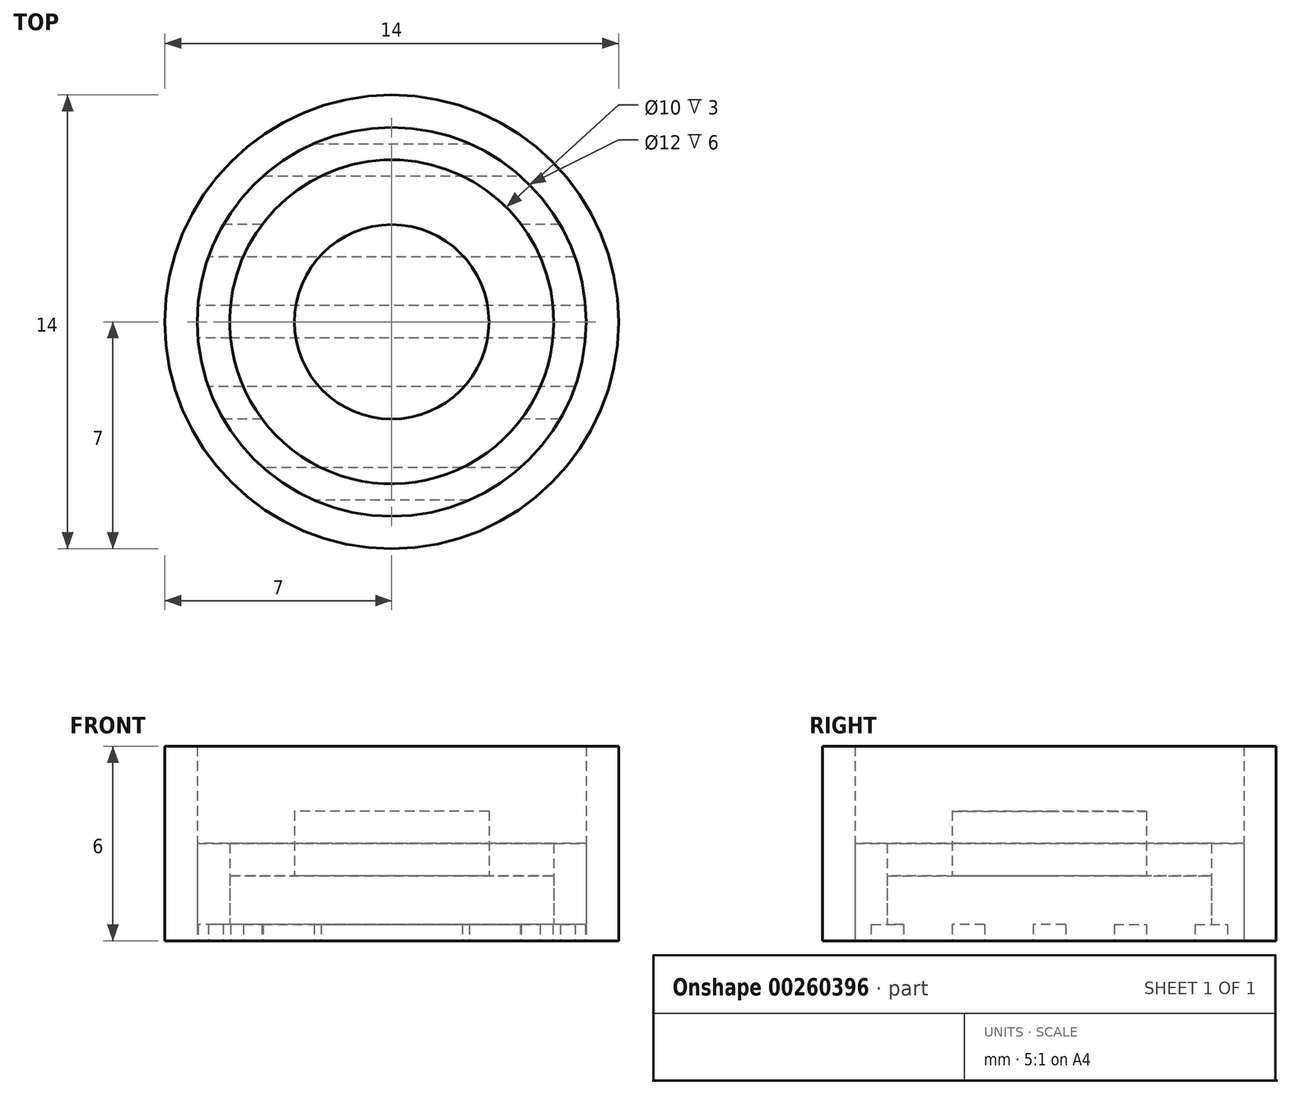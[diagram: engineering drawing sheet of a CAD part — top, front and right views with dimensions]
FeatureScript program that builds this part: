
annotation { "Feature Type Name" : "Feature", "Feature Type Description" : "" }
export const myFeature = defineFeature(function(context is Context, id is Id, definition is map)
    precondition{}
    {
        {
            var Q0;
            Q0=qCreatedBy(makeId("Top.planeOp"),FACE);
            var sketch = newSketch(context, id + "F0", { "sketchPlane" : qUnion([Q0])});
            skCircle(sketch, "E0", {"center": v(0, 0) * mm, "radius": 7 * mm});
            skCircle(sketch, "E1", {"center": v(0, 0) * mm, "radius": 5 * mm});
            skCircle(sketch, "E2", {"center": v(0, 0) * mm, "radius": 3 * mm});
            skCircle(sketch, "E3", {"center": v(0, 0) * mm, "radius": 6 * mm});
            skSolve(sketch);
        }
        {
            var Q0;
            Q0=makeQuery(id+"F0.imprint","IMPRINT",FACE,{"disambiguationData":[TD([[makeQuery(id+"F0.imprint","IMPRINT",EDGE,{"derivedFrom":sQuery(id+"F0.wireOp",EDGE,"E0")}),1.0]])]});
            extrude(context, id + "F1", {"entities" : qUnion([Q0]), "depth" : 6 * mm});
        }
        {
            var Q0;
            Q0=makeQuery(id+"F0.imprint","IMPRINT",FACE,{"disambiguationData":[TD([[makeQuery(id+"F0.imprint","IMPRINT",EDGE,{"derivedFrom":sQuery(id+"F0.wireOp",EDGE,"E1")}),1.0]])]});
            extrude(context, id + "F2", {"entities" : qUnion([Q0]), "operationType" : NewBodyOperationType.ADD, "depth" : 2 * mm});
        }
        {
            var Q0;
            Q0=makeQuery(id+"F0.imprint","IMPRINT",FACE,{"disambiguationData":[TD([[makeQuery(id+"F0.imprint","IMPRINT",EDGE,{"derivedFrom":sQuery(id+"F0.wireOp",EDGE,"E2")}),1.0]])]});
            extrude(context, id + "F3", {"entities" : qUnion([Q0]), "operationType" : NewBodyOperationType.ADD, "depth" : 4 * mm});
        }
        {
            var Q0;
            Q0=makeQuery(id+"F0.imprint","IMPRINT",FACE,{"disambiguationData":[TD([[makeQuery(id+"F0.imprint","IMPRINT",EDGE,{"derivedFrom":sQuery(id+"F0.wireOp",EDGE,"E1")}),-1.0]])]});
            extrude(context, id + "F4", {"entities" : qUnion([Q0]), "depth" : 3 * mm});
        }
        {
            var Q0;
            Q0=makeQuery(id+"F0.imprint","IMPRINT",FACE,{"disambiguationData":[TD([[makeQuery(id+"F0.imprint","IMPRINT",EDGE,{"derivedFrom":sQuery(id+"F0.wireOp",EDGE,"E0")}),1.0]])]});
            var sketch = newSketch(context, id + "F5", { "sketchPlane" : qUnion([Q0])});
            skLineSegment(sketch, "E4.bottom", {"start": v(8.2, 0.5) * mm, "end": v(-8.35, 0.5) * mm});
            skLineSegment(sketch, "E4.top", {"start": v(8.2, -0.5) * mm, "end": v(-8.35, -0.5) * mm});
            skLineSegment(sketch, "E4.left", {"start": v(8.2, 0.5) * mm, "end": v(8.2, -0.5) * mm});
            skLineSegment(sketch, "E4.right", {"start": v(-8.35, 0.5) * mm, "end": v(-8.35, -0.5) * mm});
            skLineSegment(sketch, "E5.bottom", {"start": v(8.2, 2) * mm, "end": v(-8.35, 2) * mm});
            skLineSegment(sketch, "E5.top", {"start": v(8.2, 3) * mm, "end": v(-8.35, 3) * mm});
            skLineSegment(sketch, "E5.left", {"start": v(8.2, 2) * mm, "end": v(8.2, 3) * mm});
            skLineSegment(sketch, "E5.right", {"start": v(-8.35, 2) * mm, "end": v(-8.35, 3) * mm});
            skLineSegment(sketch, "E6.bottom", {"start": v(-8.35, 4.5) * mm, "end": v(8.2, 4.5) * mm});
            skLineSegment(sketch, "E6.top", {"start": v(-8.35, 5.5) * mm, "end": v(8.2, 5.5) * mm});
            skLineSegment(sketch, "E6.left", {"start": v(-8.35, 4.5) * mm, "end": v(-8.35, 5.5) * mm});
            skLineSegment(sketch, "E6.right", {"start": v(8.2, 4.5) * mm, "end": v(8.2, 5.5) * mm});
            skPoint(sketch, "E7.firstSnap0", {"position": v(8.2, 5) * mm});
            skLineSegment(sketch, "E7.bottom", {"start": v(8.2, -2) * mm, "end": v(-8.35, -2) * mm});
            skLineSegment(sketch, "E7.top", {"start": v(8.2, -3) * mm, "end": v(-8.35, -3) * mm});
            skLineSegment(sketch, "E7.left", {"start": v(8.2, -2) * mm, "end": v(8.2, -3) * mm});
            skLineSegment(sketch, "E7.right", {"start": v(-8.35, -2) * mm, "end": v(-8.35, -3) * mm});
            skLineSegment(sketch, "E8.bottom", {"start": v(8.2, -4.5) * mm, "end": v(-8.35, -4.5) * mm});
            skLineSegment(sketch, "E8.top", {"start": v(8.2, -5.5) * mm, "end": v(-8.35, -5.5) * mm});
            skLineSegment(sketch, "E8.left", {"start": v(8.2, -4.5) * mm, "end": v(8.2, -5.5) * mm});
            skLineSegment(sketch, "E8.right", {"start": v(-8.35, -4.5) * mm, "end": v(-8.35, -5.5) * mm});
            skSolve(sketch);
        }
        {
            var Q0;
            {var subQ0=sQuery(id+"F5.wireOp",EDGE,"E5.bottom");var subQ1=makeQuery(id+"F0.imprint","IMPRINT",EDGE,{"derivedFrom":sQuery(id+"F0.wireOp",EDGE,"E3")});var subQ2=makeQuery(id+"F5.imprint","INTERSECT",VERTEX,{"disambiguationData":[OD(0.0)],"derivedFrom":[subQ1,subQ0]});Q0=makeQuery(id+"F5.imprint","IMPRINT",FACE,{"disambiguationData":[TD([[makeQuery(id+"F5.imprint","IMPRINT",EDGE,{"disambiguationData":[TD([[subQ2,-1.0]])],"derivedFrom":subQ0}),-1.0]])]});}
            var Q1;
            {var subQ0=sQuery(id+"F5.wireOp",EDGE,"E6.bottom");var subQ1=makeQuery(id+"F0.imprint","IMPRINT",EDGE,{"derivedFrom":sQuery(id+"F0.wireOp",EDGE,"E3")});var subQ2=makeQuery(id+"F5.imprint","INTERSECT",VERTEX,{"disambiguationData":[OD(0.0)],"derivedFrom":[subQ1,subQ0]});Q1=makeQuery(id+"F5.imprint","IMPRINT",FACE,{"disambiguationData":[TD([[makeQuery(id+"F5.imprint","IMPRINT",EDGE,{"disambiguationData":[TD([[subQ2,-1.0]])],"derivedFrom":subQ0}),1.0]])]});}
            var Q2;
            {var subQ0=sQuery(id+"F5.wireOp",EDGE,"E4.bottom");var subQ1=makeQuery(id+"F0.imprint","IMPRINT",EDGE,{"derivedFrom":sQuery(id+"F0.wireOp",EDGE,"E3")});var subQ2=makeQuery(id+"F5.imprint","INTERSECT",VERTEX,{"disambiguationData":[OD(0.0)],"derivedFrom":[subQ1,subQ0]});Q2=makeQuery(id+"F5.imprint","IMPRINT",FACE,{"disambiguationData":[TD([[makeQuery(id+"F5.imprint","IMPRINT",EDGE,{"disambiguationData":[TD([[subQ2,-1.0]])],"derivedFrom":subQ0}),1.0]])]});}
            var Q3;
            {var subQ0=sQuery(id+"F5.wireOp",EDGE,"E7.bottom");var subQ1=makeQuery(id+"F0.imprint","IMPRINT",EDGE,{"derivedFrom":sQuery(id+"F0.wireOp",EDGE,"E3")});var subQ2=makeQuery(id+"F5.imprint","INTERSECT",VERTEX,{"disambiguationData":[OD(0.0)],"derivedFrom":[subQ1,subQ0]});Q3=makeQuery(id+"F5.imprint","IMPRINT",FACE,{"disambiguationData":[TD([[makeQuery(id+"F5.imprint","IMPRINT",EDGE,{"disambiguationData":[TD([[subQ2,-1.0]])],"derivedFrom":subQ0}),1.0]])]});}
            var Q4;
            {var subQ0=sQuery(id+"F5.wireOp",EDGE,"E8.bottom");var subQ1=makeQuery(id+"F0.imprint","IMPRINT",EDGE,{"derivedFrom":sQuery(id+"F0.wireOp",EDGE,"E3")});var subQ2=makeQuery(id+"F5.imprint","INTERSECT",VERTEX,{"disambiguationData":[OD(0.0)],"derivedFrom":[subQ1,subQ0]});Q4=makeQuery(id+"F5.imprint","IMPRINT",FACE,{"disambiguationData":[TD([[makeQuery(id+"F5.imprint","IMPRINT",EDGE,{"disambiguationData":[TD([[subQ2,-1.0]])],"derivedFrom":subQ0}),1.0]])]});}
            extrude(context, id + "F6", {"entities" : qUnion([Q0, Q1, Q2, Q3, Q4]), "operationType" : NewBodyOperationType.REMOVE, "depth" : 0.5 * mm});
        }
    });
